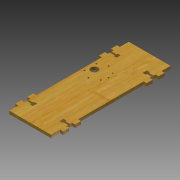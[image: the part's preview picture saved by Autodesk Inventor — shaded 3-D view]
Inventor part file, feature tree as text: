
AUTODESK INVENTOR PART (.ipt)
format: ipt  version: 2014 (Build 180170000, 170)  size: 307,712 bytes
history: native  units: mm
features: extrude x9, hole x6, sketch x4
ambient origin geometry x8: Origin, YZ Plane, XZ Plane, XY Plane, X Axis, Y Axis, Z Axis, Center Point
bodies: Solid1 (feature_tree)
feature tree (19):
  extrude  "Extrusion1"  Depth=200.0mm
  sketch  "Sketch3"  dims[d2=5.0mm d3=0.0mm d35=3.0mm]
  extrude  "Extrusion3"  Depth=3.0mm
  extrude  "Extrusion4"  Depth=2.0mm
  extrude  "Extrusion14"  Depth=5.0mm TaperAngle=0.0deg
  extrude  "Extrusion15"  Depth=5.0mm TaperAngle=0.0deg
  extrude  "Extrusion22"  Depth=1.5mm
  hole  "Hole1"  [1 undecoded]
  hole  "Hole2"  [1 undecoded]
  hole  "Hole3"  [1 undecoded]
  hole  "Hole4"  [1 undecoded]
  hole  "Hole5"  [1 undecoded]
  hole  "Hole6"  [1 undecoded]
  extrude  "Extrusion26"  Depth=8.0mm
  extrude  "Extrusion28"  Depth=1.5mm
  extrude  "Extrusion30"  Depth=1.5mm
  sketch  "Sketch1"  dims[d0=70.0mm d1=200.0mm]
  sketch  "Sketch5"  dims[d41=5.0mm d53=2.0mm]
  sketch  "Sketch6"  dims[d55=5.0mm d72=5.0mm d73=0.0mm d74=5.0mm d75=0.0mm d92=1.5mm d94=1.5mm d95=2.0mm d97=8.0mm d99=5.0mm d103=1.5mm d104=1.5mm d105=8.0mm d113=1.5mm d114=1.5mm d115=8.0mm d116=5.0mm d117=2.0mm d118=2.0mm d130=1.5mm d131=8.0mm d132=2.0mm d133=5.0mm d134=3.5mm d135=5.0mm d136=2.0mm d145=1.5mm d146=8.0mm d147=2.0mm d148=5.0mm d149=1.5mm d150=8.0mm d151=2.0mm d152=5.0mm d153=5.0mm d154=0.0mm d155=5.0mm d156=0.0mm d169=19.0mm d171=12.0mm d172=5.0mm d173=0.0mm d176=2.5mm d179=3.176mm d180=9.842mm d181=9.842mm d182=2.5mm d183=2.5mm d184=16.95mm d185=16.95mm d186=16.95mm d187=2.5mm d188=2.5mm d196=13.774mm d197=2.5mm d200=2.5mm d201=6.0mm d202=4.0mm d203=2.0mm d204=90.0deg d205=8.0mm d206=20.594885mm d207=2.5mm d208=6.0mm d209=4.0mm d210=2.0mm d211=90.0deg d212=8.0mm d213=20.594885mm d214=2.5mm d215=6.0mm d216=4.0mm d217=2.0mm d218=90.0deg d219=8.0mm d220=20.594885mm d221=2.5mm d222=6.0mm d223=4.0mm d224=2.0mm d225=90.0deg d226=8.0mm d227=20.594885mm d228=2.5mm d229=6.0mm d230=4.0mm d231=2.0mm d232=90.0deg d233=8.0mm d234=20.594885mm d235=2.5mm d236=6.0mm d237=4.0mm d238=2.0mm d239=90.0deg d240=8.0mm d241=20.594885mm d242=15.0mm d243=10.0mm d244=10.0mm d245=10.0mm d247=10.0mm d248=10.0mm d249=10.0mm d250=5.0mm d251=0.0mm d253=10.0mm d254=5.0mm d255=10.0mm d256=10.0mm d259=10.0mm d260=10.0mm d261=10.0mm d266=110.0mm d267=5.0mm d268=0.0mm d269=110.0mm d273=69.0mm d274=5.0mm d275=0.0mm]
note: 6 required parameter values undecoded (feature->parameter linkage not recoverable at this tier; creation-order binding heuristic only, values carry confidence <= 0.55)
